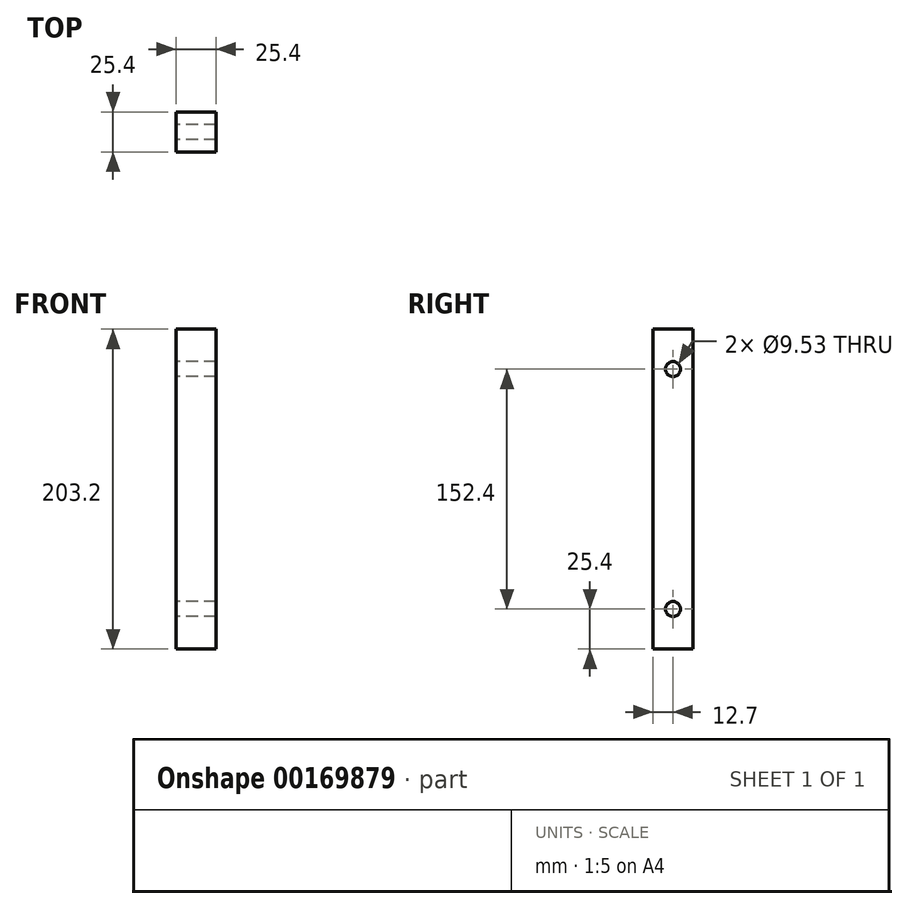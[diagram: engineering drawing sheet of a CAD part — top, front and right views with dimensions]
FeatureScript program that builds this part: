
annotation { "Feature Type Name" : "Feature", "Feature Type Description" : "" }
export const myFeature = defineFeature(function(context is Context, id is Id, definition is map)
    precondition{}
    {
        {
            var Q0;
            Q0=qCreatedBy(makeId("Right.planeOp"),FACE);
            var sketch = newSketch(context, id + "F0", { "sketchPlane" : qUnion([Q0])});
            skLineSegment(sketch, "E0.bottom", {"start": v(-12.7, -101.6) * mm, "end": v(12.7, -101.6) * mm});
            skLineSegment(sketch, "E0.top", {"start": v(-12.7, 101.6) * mm, "end": v(12.7, 101.6) * mm});
            skLineSegment(sketch, "E0.left", {"start": v(-12.7, -101.6) * mm, "end": v(-12.7, 101.6) * mm});
            skLineSegment(sketch, "E0.right", {"start": v(12.7, -101.6) * mm, "end": v(12.7, 101.6) * mm});
            skPoint(sketch, "E0.middle", {"position": v(0, 0) * mm});
            skLineSegment(sketch, "E1", {"start": v(0, 101.6) * mm, "end": v(0, -101.6) * mm, "construction": true});
            skLineSegment(sketch, "E2", {"start": v(12.7, 0) * mm, "end": v(0, 0) * mm, "construction": true});
            skCircle(sketch, "E3", {"center": v(0, -76.2) * mm, "radius": 4.76 * mm});
            skCircle(sketch, "E4.MirrorC", {"center": v(0, 76.2) * mm, "radius": 4.76 * mm});
            skSolve(sketch);
        }
        {
            var Q0;
            Q0 = qSketchRegion(id + "F0", true);
            extrude(context, id + "F1", {"entities" : qUnion([Q0]), "depth" : 25.4 * mm});
        }
    });
